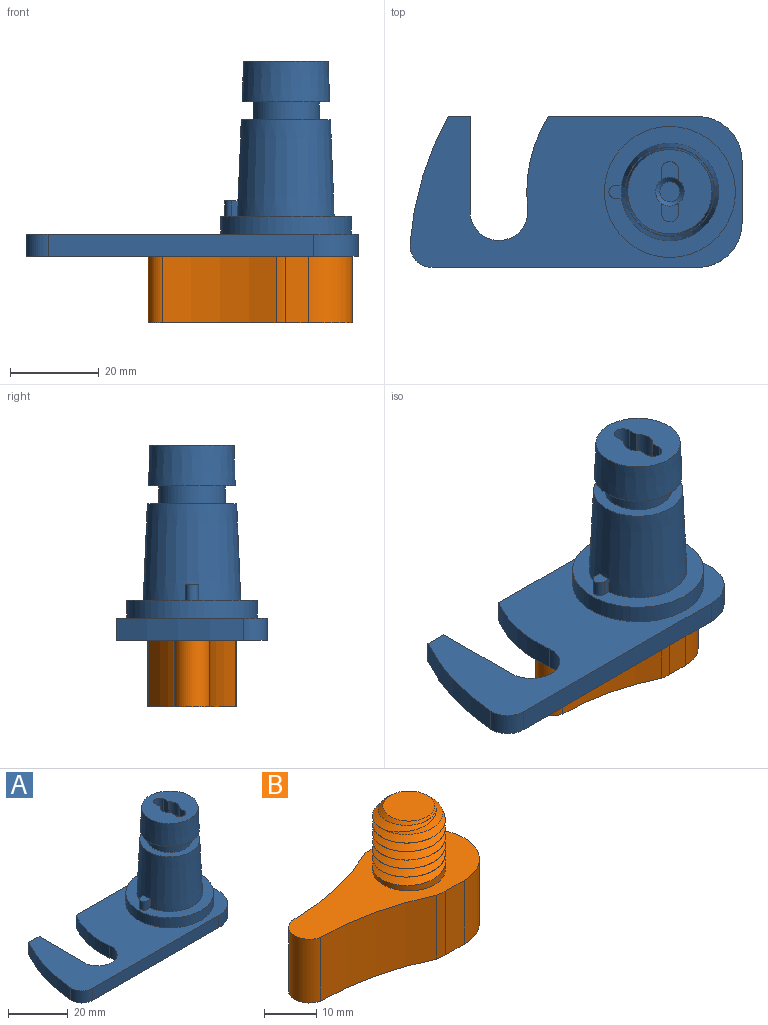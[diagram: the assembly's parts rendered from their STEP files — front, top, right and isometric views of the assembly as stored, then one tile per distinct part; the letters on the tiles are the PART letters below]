
ASSEMBLY  parts=2 mates=3
PART A: 42 faces, bbox 74.8x34x45 mm
  f0: cylinder r=5.9mm len=13mm, axis (0,0,-1), area 6.3mm2, adj f37,f38,f39,f40,f41
  f1: plane 74.81x34mm, normal (0,0,1), area 1355mm2, adj f2,f3,f8,f9,f11,f30,f31,f32
  f2: plane 5x5mm, normal (0,1,0), area 25mm2, adj f1,f10,f31,f33
  f3: plane 33.66x5mm, normal (0,1,0), area 168.3mm2, adj f1,f10,f30,f35
  f4: plane 19x19mm, normal (0,0,1), area 224mm2, adj f5,f15,f22,f23,f24,f25,f27,f28
  f5: cylinder r=3.25mm len=12mm, axis (0,0,1), area 176.1mm2, adj f4,f21,f22,f23,f24,f25,f26,f29
  f6: plane 29.5x29.5mm, normal (0,0,1), area 296mm2, adj f7,f11,f16,f17,f19
  f7: cone r=11mm half-angle=2.5deg, axis (0,0,-1), area 1433.5mm2, adj f6,f13,f16,f17,f18
  f8: plane 59.81x5mm, normal (0,-1,0), area 299mm2, adj f1,f10,f34,f36
  f9: plane 14x5mm, normal (1,0,0), area 70mm2, adj f1,f10,f34,f35
  f10: plane 74.81x34mm, normal (0,0,-1), area 1842.4mm2, adj f2,f3,f8,f9,f30,f31,f32,f33
  f11: cylinder r=14.75mm len=29.5mm, axis (0,0,-1), area 370.7mm2, adj f1,f6
  f12: cylinder r=7.5mm len=15mm, axis (0,0,1), area 188.5mm2, adj f13,f14
  f13: plane 20.13x20.13mm, normal (0,0,1), area 141.6mm2, adj f7,f12
  f14: plane 19.79x19.79mm, normal (0,0,-1), area 130.8mm2, adj f12,f15
  f15: cone r=11mm half-angle=2.5deg, axis (0,0,-1), area 561.1mm2, adj f4,f14
  f16: plane 3.5x1.5mm, normal (0,-1,0), area 5mm2, adj f6,f7,f18,f19
  f17: plane 3.5x1.5mm, normal (0,1,0), area 5mm2, adj f6,f7,f18,f19
  f18: plane 3x3mm, normal (0,0,1), area 7.8mm2, adj f7,f16,f17,f19
  f19: cylinder r=1.5mm len=3.5mm, axis (0,0,1), area 16.5mm2, adj f6,f16,f17,f18
  f20: plane 4.5x4.5mm, normal (0,0,1), area 15.9mm2, adj f29
  f21: plane 4.19x4mm, normal (0,0,1), area 13.2mm2, adj f5,f22,f23,f28
  f22: plane 8x2.19mm, normal (-1,0,0), area 17.5mm2, adj f4,f5,f21,f28
  f23: plane 8x2.19mm, normal (1,0,0), area 17.5mm2, adj f4,f5,f21,f28
  f24: plane 8x2.19mm, normal (1,0,0), area 17.5mm2, adj f4,f5,f26,f27
  f25: plane 8x2.19mm, normal (-1,0,0), area 17.5mm2, adj f4,f5,f26,f27
  f26: plane 4.19x4mm, normal (0,0,1), area 13.2mm2, adj f5,f24,f25,f27
  f27: cylinder r=2mm len=8mm, axis (0,0,-1), area 50.3mm2, adj f4,f24,f25,f26
  f28: cylinder r=2mm len=8mm, axis (0,0,-1), area 50.3mm2, adj f4,f21,f22,f23
  f29: cone r=2.25mm half-angle=45deg, axis (0,0,1), area 24.4mm2, adj f5,f20
  f30: cylinder r=32.25mm len=20.68mm, axis (0,0,1), area 108mm2, adj f1,f3,f10,f32
  f31: plane 22.17x5mm, normal (1,0,0), area 110.8mm2, adj f1,f2,f10,f32
  f32: cylinder r=6.5mm len=12.96mm, axis (0,0,1), area 102.1mm2, adj f1,f10,f30,f31
  f33: cylinder r=70.11mm len=28.62mm, axis (0,0,1), area 150.5mm2, adj f1,f2,f10,f36
  f34: cylinder r=10mm len=10mm, axis (0,0,-1), area 78.5mm2, adj f1,f8,f9,f10
  f35: cylinder r=10mm len=10mm, axis (0,0,1), area 78.5mm2, adj f1,f3,f9,f10
  f36: cylinder r=5mm len=5.38mm, axis (0,0,1), area 41.2mm2, adj f1,f8,f10,f33
  f37: plane 11.8x11.8mm, normal (0,0,-1), area 109.4mm2, adj f0
  f38: cone r=5.9mm half-angle=45deg, axis (0,0,-1), area 73.8mm2, adj f0,f10,f40,f41
  f39: plane 1.98x1.71mm, normal (0,-1,0), area 1.7mm2, adj f0,f40,f41
  f40: bspline ~17.59x15.23mm, area 522.6mm2, adj f0,f38,f39,f41
  f41: bspline ~17.59x15.23mm, area 567.3mm2, adj f0,f38,f39,f40
PART B: 16 faces, bbox 46x20x31 mm
  f0: cylinder r=7mm len=14mm, axis (0,0,-1), area 86.4mm2, adj f9,f12,f13,f14,f15
  f1: cylinder r=60mm len=25.67mm, axis (0,0,-1), area 398.1mm2, adj f2,f8,f9,f10
  f2: cylinder r=4mm len=15mm, axis (0,0,-1), area 161.6mm2, adj f1,f3,f9,f10
  f3: cylinder r=60mm len=25.67mm, axis (0,0,-1), area 398.1mm2, adj f2,f4,f9,f10
  f4: cylinder r=10mm len=15mm, axis (0,0,-1), area 33.6mm2, adj f3,f5,f9,f10
  f5: plane 15x5mm, normal (0,-1,0), area 75mm2, adj f4,f6,f9,f10
  f6: cylinder r=10mm len=20mm, axis (0,0,-1), area 471.2mm2, adj f5,f7,f9,f10
  f7: plane 15x5mm, normal (0,1,0), area 75mm2, adj f6,f8,f9,f10
  f8: cylinder r=10mm len=15mm, axis (0,0,-1), area 33.6mm2, adj f1,f7,f9,f10
  f9: plane 46x20mm, normal (0,0,1), area 464.2mm2, adj f0,f1,f2,f3,f4,f5,f6,f7
  f10: plane 46x20mm, normal (0,0,-1), area 618.2mm2, adj f1,f2,f3,f4,f5,f6,f7,f8
  f11: plane 10x10mm, normal (0,0,1), area 78.5mm2, adj f12
  f12: cone r=5mm half-angle=45deg, axis (0,0,-1), area 57.7mm2, adj f0,f11,f14,f15
  f13: plane 1.99x1.72mm, normal (0,1,0), area 1.7mm2, adj f0,f14,f15
  f14: bspline ~16.17x15mm, area 476.7mm2, adj f0,f12,f13,f15
  f15: bspline ~16.17x15mm, area 515.7mm2, adj f0,f12,f13,f14
PLACE A t=(-19,29.29,-7.71)mm
PLACE B t=(-118.4,29.29,-22.71)mm
MATE fastened B.f0 <-> A.f0  axis (0,0,1) through (2.25,29.29,7.29)mm
MATE slider A.f35 <-> A.f10  axis (0,0,-1) through (8.5,36.29,-7.71)mm
MATE slider B.f0 <-> A.f0  axis (0,0,1) through (2.25,29.29,7.29)mm
